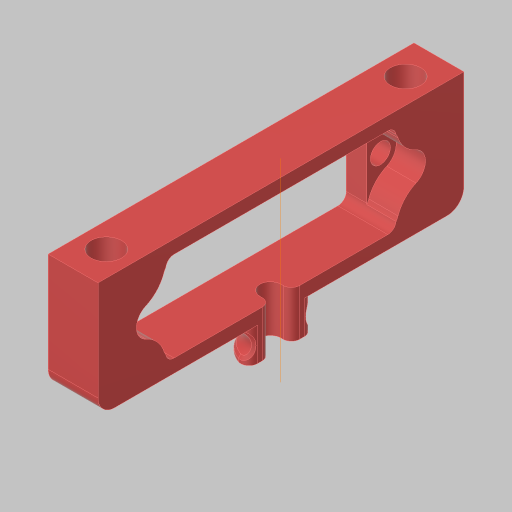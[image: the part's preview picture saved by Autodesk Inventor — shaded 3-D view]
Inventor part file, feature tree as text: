
AUTODESK INVENTOR PART (.ipt)
format: ipt  version: 2023.5 (Build 275446000, 446)  size: 274,944 bytes
history: native  units: in
note: dims shown in document units (in); Inventor stores cm internally (conversion verified against a paired STEP export)
features: sketch x6, extrude x5, fillet x4, hole x2, projected_geometry x2, other x1, revolve x1, chamfer x1
ambient origin geometry x8: Origin, YZ Plane, XZ Plane, XY Plane, X Axis, Y Axis, Z Axis, Center Point
bodies: Solid1 (feature_tree)
feature tree (22):
  extrude  "Extrusion1"  Depth=0.875in
  sketch  "Sketch2"  dims[d2=0.375in d3=0.0in d4=1.7323in]
  extrude  "Extrusion2"  Depth=1.7323in
  hole  "Hole1"  [1 undecoded]
  fillet  "Fillet1"  Radius=0.2205in
  extrude  "Extrusion4"  Depth=1.9366in
  hole  "Hole2"  [1 undecoded]
  fillet  "Fillet2"  Radius=2.25in
  extrude  "Extrusion5"  Depth=0.0625in
  fillet  "Fillet3"  Radius=0.1575in
  extrude  "Extrusion6"  Depth=0.0787in
  fillet  "Fillet4"  [1 undecoded]
  other  "Work Axis3"
  revolve  "Revolution2"  [1 undecoded]
  chamfer  "Chamfer1"  Distance=0.25in
  sketch  "Sketch1"  dims[d0=2.75in d1=0.875in]
  sketch  "Sketch5"  dims[d5=0.675in d7=0.2362in d8=0.2205in d9=0.0in]
  sketch  "Sketch7"  dims[d10=0.15in d11=0.75in d12=0.279in d13=0.25in d14=0.5635in d15=1.0in d16=0.8108in d20=1.9366in]
  sketch  "Sketch8"  dims[d21=0.125in d24=0.0in d25=0.0in d26=2.25in]
  sketch  "Sketch10"  dims[d27=0.2283in d28=0.75in d29=0.563in d30=0.12in d31=0.5635in d32=0.3in d33=0.8108in d34=0.0625in d35=0.1575in d36=0.0787in d37=0.0in d38=0.0in d39=0.0625in d40=0.25in d41=0.25in d42=0.0in d43=0.0625in d48=0.1in d49=0.0625in d50=90.0deg d51=0.0157in d52=0.125in d53=45.0deg]
  projected_geometry  "Projected Loop1"
  projected_geometry  "Project Cut Edges1"
note: 4 required parameter values undecoded (feature->parameter linkage not recoverable at this tier; creation-order binding heuristic only, values carry confidence <= 0.55)